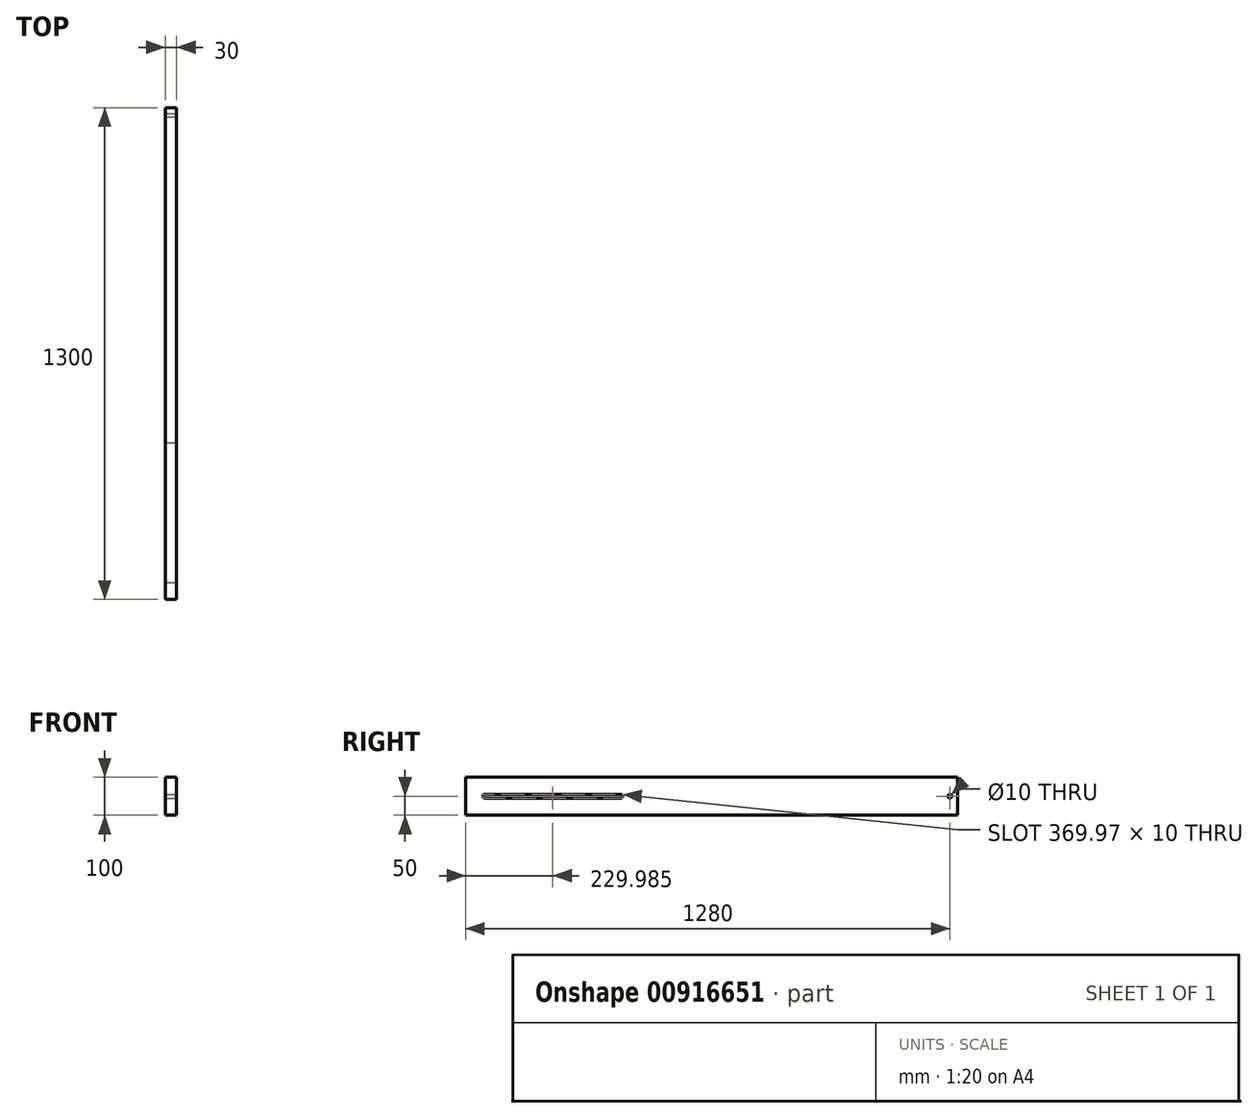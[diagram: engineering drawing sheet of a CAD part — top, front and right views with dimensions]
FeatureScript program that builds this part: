
annotation { "Feature Type Name" : "Feature", "Feature Type Description" : "" }
export const myFeature = defineFeature(function(context is Context, id is Id, definition is map)
    precondition{}
    {
        {
            var Q0;
            Q0=qCreatedBy(makeId("Front.planeOp"),FACE);
            var sketch = newSketch(context, id + "F0", { "sketchPlane" : qUnion([Q0])});
            skLineSegment(sketch, "E0.bottom", {"start": v(15, -50) * mm, "end": v(-15, -50) * mm});
            skLineSegment(sketch, "E0.top", {"start": v(15, 50) * mm, "end": v(-15, 50) * mm});
            skLineSegment(sketch, "E0.left", {"start": v(15, -50) * mm, "end": v(15, 50) * mm});
            skLineSegment(sketch, "E0.right", {"start": v(-15, -50) * mm, "end": v(-15, 50) * mm});
            skPoint(sketch, "E0.middle", {"position": v(0, 0) * mm});
            skSolve(sketch);
        }
        {
            var Q0;
            Q0=makeQuery(id+"F0.imprint","IMPRINT",FACE,{"disambiguationData":[TD([[makeQuery(id+"F0.imprint","IMPRINT",EDGE,{"derivedFrom":sQuery(id+"F0.wireOp",EDGE,"E0.bottom")}),-1.0]])]});
            extrude(context, id + "F1", {"entities" : qUnion([Q0]), "depth" : 1300 * mm, "offsetDistance" : 25 * mm});
        }
        {
            var Q0;
            Q0=makeQuery(id+"F1.opExtrude","SWEPT_FACE",FACE,{"disambiguationData":[OSD([sQuery(id+"F0.wireOp",EDGE,"E0.left")])]});
            var sketch = newSketch(context, id + "F2", { "sketchPlane" : qUnion([Q0])});
            skCircle(sketch, "E1", {"center": v(-20, 0) * mm, "radius": 5 * mm});
            skCircle(sketch, "E2", {"center": v(-1250, 0) * mm, "radius": 5 * mm});
            skPoint(sketch, "E2.centerSnap0", {"position": v(-1300, 0) * mm});
            skCircle(sketch, "E3", {"center": v(-890.03, 0) * mm, "radius": 5 * mm});
            skLineSegment(sketch, "E4", {"start": v(-890.03, -5) * mm, "end": v(-1250, -5) * mm});
            skLineSegment(sketch, "E5", {"start": v(-1250, -5) * mm, "end": v(-1250, 5) * mm});
            skLineSegment(sketch, "E6", {"start": v(-1250, 5) * mm, "end": v(-890.03, 5) * mm});
            skSolve(sketch);
        }
        {
            var Q0;
            Q0 = qSketchRegion(id + "F2", true);
            extrude(context, id + "F3", {"entities" : qUnion([Q0]), "operationType" : NewBodyOperationType.REMOVE, "endBound" : BoundingType.THROUGH_ALL, "oppositeDirection" : true, "depth" : 25 * mm, "offsetDistance" : 25 * mm});
        }
    });
